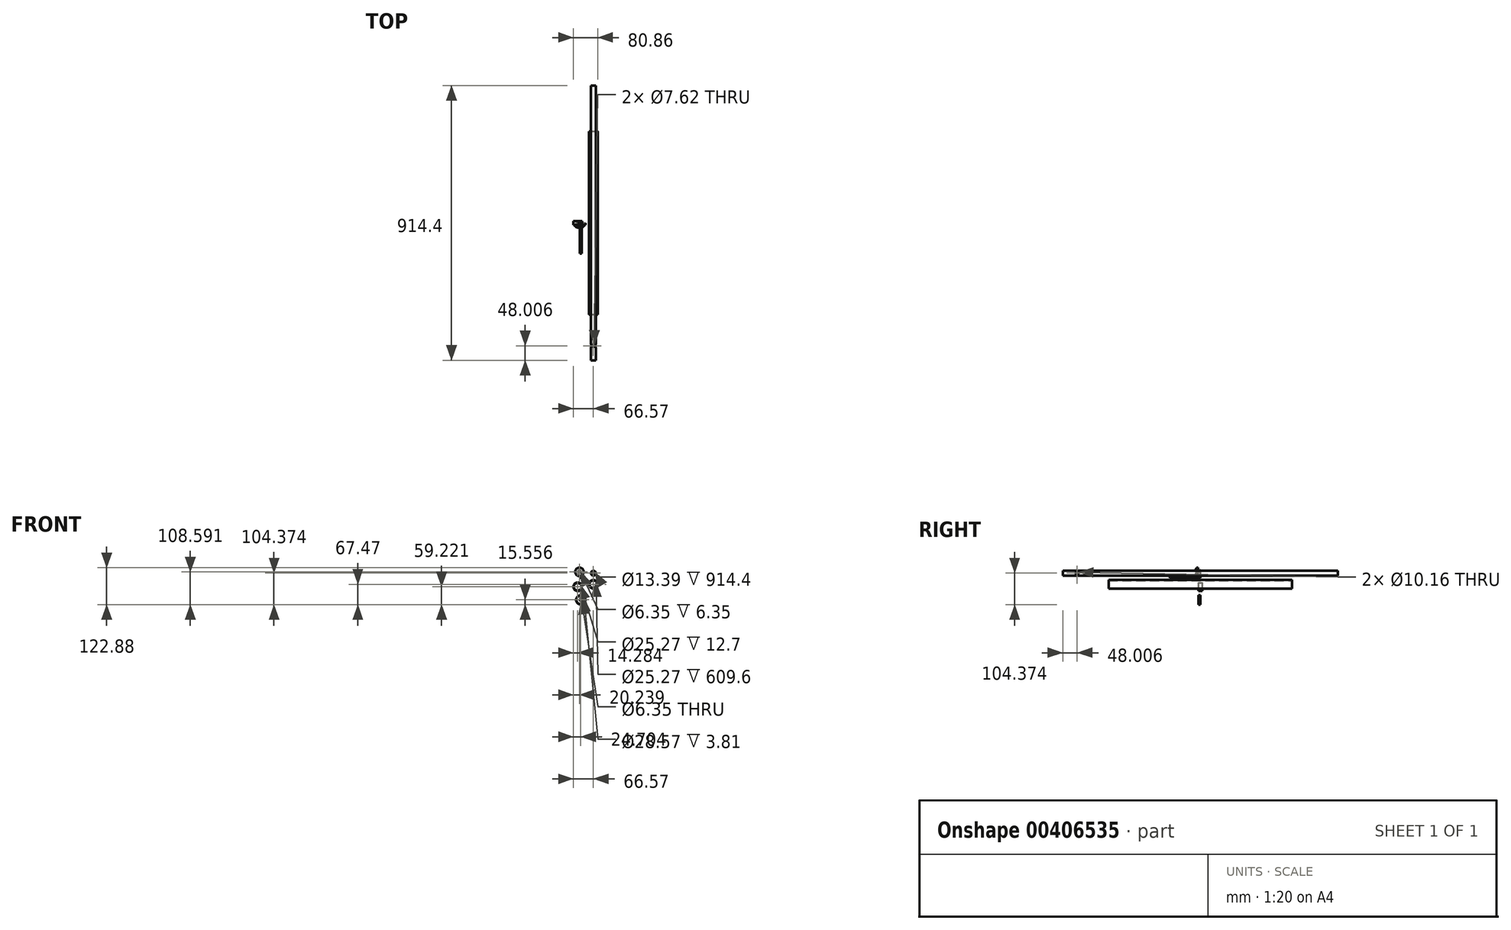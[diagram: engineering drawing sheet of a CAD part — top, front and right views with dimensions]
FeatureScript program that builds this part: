
annotation { "Feature Type Name" : "Feature", "Feature Type Description" : "" }
export const myFeature = defineFeature(function(context is Context, id is Id, definition is map)
    precondition{}
    {
        {
            var Q0;
            Q0=qCreatedBy(makeId("Front.planeOp"),FACE);
            var sketch = newSketch(context, id + "F0", { "sketchPlane" : qUnion([Q0])});
            skCircle(sketch, "E0", {"center": v(0, 0) * mm, "radius": 12.64 * mm});
            skCircle(sketch, "E1", {"center": v(0, 0) * mm, "radius": 14.29 * mm});
            skCircle(sketch, "E2", {"center": v(0, 36.9) * mm, "radius": 7.94 * mm});
            skCircle(sketch, "E3", {"center": v(0, 36.9) * mm, "radius": 6.7 * mm});
            skCircle(sketch, "E4", {"center": v(-46.33, 41.12) * mm, "radius": 14.29 * mm});
            skCircle(sketch, "E5", {"center": v(-46.33, 41.12) * mm, "radius": 3.18 * mm});
            skCircle(sketch, "E6", {"center": v(-41.37, 24) * mm, "radius": 3.18 * mm});
            skCircle(sketch, "E7", {"center": v(-52.29, -8.25) * mm, "radius": 14.29 * mm});
            skCircle(sketch, "E8", {"center": v(-52.29, -8.25) * mm, "radius": 12.64 * mm});
            skCircle(sketch, "E9", {"center": v(-41.87, -51.91) * mm, "radius": 14.29 * mm});
            skCircle(sketch, "E10", {"center": v(-41.87, -51.91) * mm, "radius": 15.56 * mm});
            skCircle(sketch, "E11", {"center": v(-41.87, -51.91) * mm, "radius": 3.18 * mm});
            skSolve(sketch);
        }
        {
            var Q0;
            Q0=makeQuery(id+"F0.imprint","IMPRINT",FACE,{"disambiguationData":[TD([[makeQuery(id+"F0.imprint","IMPRINT",EDGE,{"derivedFrom":sQuery(id+"F0.wireOp",EDGE,"E0")}),-1.0]])]});
            extrude(context, id + "F1", {"entities" : qUnion([Q0]), "endBound" : BoundingType.SYMMETRIC, "depth" : 609.6 * mm, "offsetDistance" : 25.4 * mm});
        }
        {
            var Q0;
            Q0=makeQuery(id+"F0.imprint","IMPRINT",FACE,{"disambiguationData":[TD([[makeQuery(id+"F0.imprint","IMPRINT",EDGE,{"derivedFrom":sQuery(id+"F0.wireOp",EDGE,"E2")}),1.0]])]});
            extrude(context, id + "F2", {"entities" : qUnion([Q0]), "endBound" : BoundingType.SYMMETRIC, "depth" : 914.4 * mm, "offsetDistance" : 25.4 * mm});
        }
        {
            var Q0;
            Q0=makeQuery(id+"F0.imprint","IMPRINT",FACE,{"disambiguationData":[TD([[makeQuery(id+"F0.imprint","IMPRINT",EDGE,{"derivedFrom":sQuery(id+"F0.wireOp",EDGE,"E4")}),1.0]])]});
            extrude(context, id + "F3", {"entities" : qUnion([Q0]), "depth" : 12.7 * mm, "offsetDistance" : 25.4 * mm});
        }
        {
            var Q0;
            Q0=makeQuery(id+"F0.imprint","IMPRINT",FACE,{"disambiguationData":[TD([[makeQuery(id+"F0.imprint","IMPRINT",EDGE,{"derivedFrom":sQuery(id+"F0.wireOp",EDGE,"E5")}),1.0]])]});
            extrude(context, id + "F4", {"entities" : qUnion([Q0]), "operationType" : NewBodyOperationType.ADD, "depth" : 6.35 * mm, "offsetDistance" : 25.4 * mm});
        }
        {
            var Q0;
            Q0=makeQuery(id+"F3.opExtrude","CAP_EDGE",EDGE,{"disambiguationData":[OSD([sQuery(id+"F0.wireOp",EDGE,"E4")])],"isStart":true});
            fillet(context, id + "F5", {"entities" : qUnion([Q0]), "radius" : 7.62 * mm, "tangentPropagation" : true, "allowEdgeOverflow" : false});
        }
        {
            var Q0;
            Q0=makeQuery(id+"F0.imprint","IMPRINT",FACE,{"disambiguationData":[TD([[makeQuery(id+"F0.imprint","IMPRINT",EDGE,{"derivedFrom":sQuery(id+"F0.wireOp",EDGE,"E6")}),1.0]])]});
            extrude(context, id + "F6", {"entities" : qUnion([Q0]), "depth" : 101.6 * mm, "offsetDistance" : 25.4 * mm});
        }
        {
            var Q0;
            Q0=makeQuery(id+"F0.imprint","IMPRINT",FACE,{"disambiguationData":[TD([[makeQuery(id+"F0.imprint","IMPRINT",EDGE,{"derivedFrom":sQuery(id+"F0.wireOp",EDGE,"E7")}),1.0]])]});
            extrude(context, id + "F7", {"entities" : qUnion([Q0]), "endBound" : BoundingType.SYMMETRIC, "depth" : 12.7 * mm, "offsetDistance" : 25.4 * mm});
        }
        {
            var Q0;
            Q0=makeQuery(id+"F0.imprint","IMPRINT",FACE,{"disambiguationData":[TD([[makeQuery(id+"F0.imprint","IMPRINT",EDGE,{"derivedFrom":sQuery(id+"F0.wireOp",EDGE,"E9")}),1.0]])]});
            extrude(context, id + "F8", {"entities" : qUnion([Q0]), "depth" : 2.54 * mm, "offsetDistance" : 25.4 * mm});
        }
        {
            var Q0;
            Q0=makeQuery(id+"F0.imprint","IMPRINT",FACE,{"disambiguationData":[TD([[makeQuery(id+"F0.imprint","IMPRINT",EDGE,{"derivedFrom":sQuery(id+"F0.wireOp",EDGE,"E9")}),-1.0]])]});
            extrude(context, id + "F9", {"entities" : qUnion([Q0]), "operationType" : NewBodyOperationType.ADD, "depth" : 6.35 * mm, "offsetDistance" : 25.4 * mm});
        }
        {
            var Q0;
            Q0=qCreatedBy(makeId("Right.planeOp"),FACE);
            var sketch = newSketch(context, id + "F10", { "sketchPlane" : qUnion([Q0])});
            skPoint(sketch, "E12", {"position": v(-409.2, 0) * mm});
            skPoint(sketch, "E13", {"position": v(-409.2, 36.9) * mm});
            skCircle(sketch, "E14", {"center": v(-409.2, 36.9) * mm, "radius": 5.08 * mm});
            skSolve(sketch);
        }
        {
            var Q0;
            Q0=makeQuery(id+"F10.imprint","IMPRINT",FACE,{"disambiguationData":[TD([[makeQuery(id+"F10.imprint","IMPRINT",EDGE,{"derivedFrom":sQuery(id+"F10.wireOp",EDGE,"E14")}),1.0]])]});
            extrude(context, id + "F11", {"entities" : qUnion([Q0]), "operationType" : NewBodyOperationType.REMOVE, "endBound" : BoundingType.SYMMETRIC, "oppositeDirection" : true, "depth" : 25.4 * mm, "offsetDistance" : 25.4 * mm});
        }
        {
            var Q0;
            Q0=qCreatedBy(makeId("Top.planeOp"),FACE);
            var sketch = newSketch(context, id + "F12", { "sketchPlane" : qUnion([Q0])});
            skPoint(sketch, "E15", {"position": v(0, -409.2) * mm});
            skCircle(sketch, "E16", {"center": v(0, -409.2) * mm, "radius": 3.81 * mm});
            skSolve(sketch);
        }
        {
            var Q0;
            Q0=makeQuery(id+"F12.imprint","IMPRINT",FACE,{"disambiguationData":[TD([[makeQuery(id+"F12.imprint","IMPRINT",EDGE,{"derivedFrom":sQuery(id+"F12.wireOp",EDGE,"E16")}),1.0]])]});
            extrude(context, id + "F13", {"entities" : qUnion([Q0]), "operationType" : NewBodyOperationType.REMOVE, "endBound" : BoundingType.THROUGH_ALL, "depth" : 25.4 * mm, "offsetDistance" : 25.4 * mm});
        }
    });
